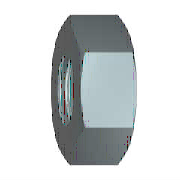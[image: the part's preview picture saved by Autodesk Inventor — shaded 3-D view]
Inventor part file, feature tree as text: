
AUTODESK INVENTOR PART (.ipt)
format: ipt  version: 2014 SP1 (Build 180222100, 222)  size: 172,032 bytes
history: native  units: mm (DEFAULTED — no unit token found)
features: sketch x3, chamfer x1, hole x1, other x1, plane x1
ambient origin geometry x7: Origin, YZ Plane, XZ Plane, X Axis, Y Axis, Z Axis, Center Point
bodies: Solid1 (feature_tree), Body (feature_tree)
feature tree (7):
  chamfer  "Chamfer1"  Angle=30.0deg  [1 undecoded]
  hole  "Thread"  [1 undecoded]
  other  "Work Axis1"
  plane  "Work Plane1"
  sketch  "Sketch1"  dims[d0=11.547005mm]
  sketch  "Sketch2"  dims[d1=5.7mm]
  sketch  "Sketch3"  dims[d2=0.0mm d3=30.0deg d4=30.0deg d5=10.0mm d6=10.0mm d7=90.0deg d25=4.917mm d26=6.0mm d27=4.0mm d28=2.0mm d29=14.3117mm d30=8.0mm d31=20.594885mm d8=0.541266mm d9=30.0deg d10=0.541266mm d11=30.0deg d13=0.0mm d14=0.0mm d39=0.0mm d40=0.541266mm d41=0.541266mm d42=0.0mm]
note: 2 required parameter values undecoded (feature->parameter linkage not recoverable at this tier; creation-order binding heuristic only, values carry confidence <= 0.55)
